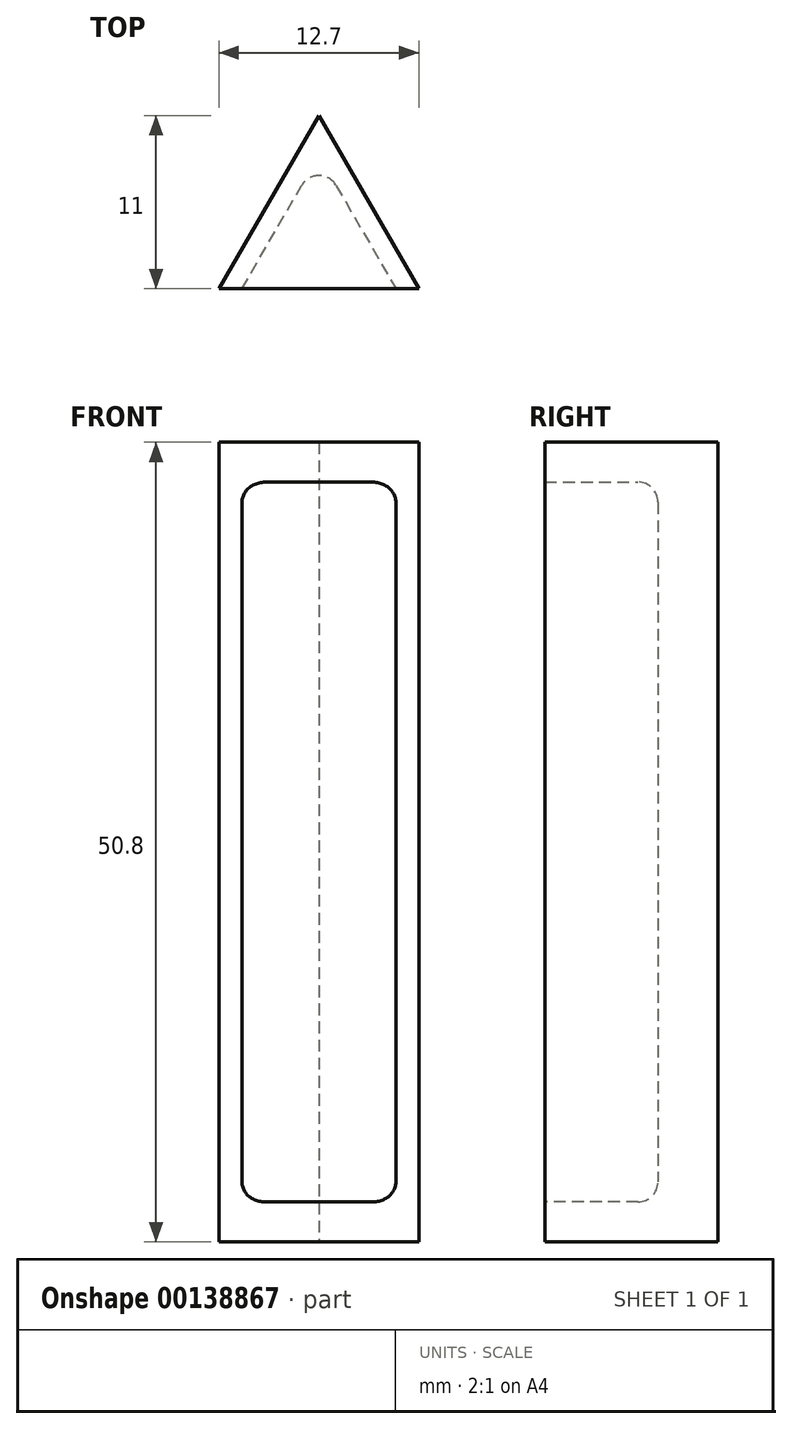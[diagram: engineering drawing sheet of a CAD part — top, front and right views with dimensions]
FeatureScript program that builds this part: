
annotation { "Feature Type Name" : "Feature", "Feature Type Description" : "" }
export const myFeature = defineFeature(function(context is Context, id is Id, definition is map)
    precondition{}
    {
        {
            var Q0;
            Q0=qCreatedBy(makeId("Top.planeOp"),FACE);
            var sketch = newSketch(context, id + "F0", { "sketchPlane" : qUnion([Q0])});
            skLineSegment(sketch, "E0", {"start": v(0, 0) * mm, "end": v(0, 11) * mm});
            skLineSegment(sketch, "E1", {"start": v(0, 11) * mm, "end": v(6.35, 0) * mm});
            skLineSegment(sketch, "E2", {"start": v(6.35, 0) * mm, "end": v(-6.35, 0) * mm});
            skLineSegment(sketch, "E3", {"start": v(-6.35, 0) * mm, "end": v(0, 11) * mm});
            skSolve(sketch);
        }
        {
            var Q0;
            {var subQ0=sQuery(id+"F0.wireOp",EDGE,"E0");Q0=makeQuery(id+"F0.imprint","IMPRINT",FACE,{"disambiguationData":[TD([[makeQuery(id+"F0.imprint","IMPRINT",EDGE,{"derivedFrom":subQ0}),1.0]])]});}
            var Q1;
            {var subQ0=sQuery(id+"F0.wireOp",EDGE,"E0");Q1=makeQuery(id+"F0.imprint","IMPRINT",FACE,{"disambiguationData":[TD([[makeQuery(id+"F0.imprint","IMPRINT",EDGE,{"derivedFrom":subQ0}),-1.0]])]});}
            extrude(context, id + "F1", {"entities" : qUnion([Q0, Q1]), "depth" : 50.8 * mm});
        }
        {
            var Q0;
            Q0=makeQuery(id+"F1.opExtrude","CAP_FACE",FACE,{"disambiguationData":[OSD([sQuery(id+"F0.wireOp",EDGE,"E1"),sQuery(id+"F0.wireOp",EDGE,"E2"),sQuery(id+"F0.wireOp",EDGE,"E3")])],"isStart":false});
            cPlane(context, id + "F2", {"entities" : qUnion([Q0]), "cplaneType" : CPlaneType.OFFSET, "offset" : 2.54 * mm, "oppositeDirection" : true, "width" : 152.4 * mm, "height" : 152.4 * mm});
        }
        {
            var Q0;
            Q0=qCreatedBy(id+"F2.planeOp",FACE);
            var sketch = newSketch(context, id + "F3", { "sketchPlane" : qUnion([Q0])});
            skLineSegment(sketch, "E4.0", {"start": v(-4.15, 1.27) * mm, "end": v(0, 8.46) * mm});
            skLineSegment(sketch, "E4.1", {"start": v(4.15, 1.27) * mm, "end": v(-4.15, 1.27) * mm});
            skLineSegment(sketch, "E4.2", {"start": v(0, 8.46) * mm, "end": v(4.15, 1.27) * mm});
            skLineSegment(sketch, "E5", {"start": v(-4.15, 1.27) * mm, "end": v(-4.88, 0) * mm});
            skLineSegment(sketch, "E6", {"start": v(-4.88, 0) * mm, "end": v(4.88, 0) * mm});
            skLineSegment(sketch, "E7", {"start": v(4.88, 0) * mm, "end": v(4.15, 1.27) * mm});
            skSolve(sketch);
        }
        {
            var Q0;
            Q0=makeQuery(id+"F3.imprint","IMPRINT",FACE,{"disambiguationData":[TD([[makeQuery(id+"F3.imprint","IMPRINT",EDGE,{"derivedFrom":sQuery(id+"F3.wireOp",EDGE,"E4.0")}),-1.0]])]});
            var Q1;
            Q1=makeQuery(id+"F3.imprint","IMPRINT",FACE,{"disambiguationData":[TD([[makeQuery(id+"F3.imprint","IMPRINT",EDGE,{"derivedFrom":sQuery(id+"F3.wireOp",EDGE,"E4.1")}),1.0]])]});
            extrude(context, id + "F4", {"entities" : qUnion([Q0, Q1]), "operationType" : NewBodyOperationType.REMOVE, "oppositeDirection" : true, "depth" : 45.72 * mm});
        }
        {
            var Q0;
            Q0=makeQuery(id+"F4.boolean.opBoolean","COPY",EDGE,{"derivedFrom":makeQuery(id+"F4.opExtrude","SWEPT_EDGE",EDGE,{"disambiguationData":[OSD([sQuery(id+"F3.wireOp",EDGE,"E4.0"),sQuery(id+"F3.wireOp",EDGE,"E4.2")])]})});
            var Q1;
            Q1=makeQuery(id+"F4.boolean.opBoolean","COPY",EDGE,{"derivedFrom":makeQuery(id+"F4.opExtrude","CAP_EDGE",EDGE,{"disambiguationData":[OSD([sQuery(id+"F3.wireOp",EDGE,"E4.2"),sQuery(id+"F3.wireOp",EDGE,"E7")])],"isStart":false})});
            var Q2;
            Q2=makeQuery(id+"F4.boolean.opBoolean","COPY",EDGE,{"derivedFrom":makeQuery(id+"F4.opExtrude","CAP_EDGE",EDGE,{"disambiguationData":[OSD([sQuery(id+"F3.wireOp",EDGE,"E4.0"),sQuery(id+"F3.wireOp",EDGE,"E5")])],"isStart":false})});
            var Q3;
            Q3=makeQuery(id+"F4.boolean.opBoolean","COPY",EDGE,{"derivedFrom":makeQuery(id+"F4.opExtrude","CAP_EDGE",EDGE,{"disambiguationData":[OSD([sQuery(id+"F3.wireOp",EDGE,"E4.0"),sQuery(id+"F3.wireOp",EDGE,"E5")])],"isStart":true})});
            var Q4;
            Q4=makeQuery(id+"F4.boolean.opBoolean","COPY",EDGE,{"derivedFrom":makeQuery(id+"F4.opExtrude","CAP_EDGE",EDGE,{"disambiguationData":[OSD([sQuery(id+"F3.wireOp",EDGE,"E4.2"),sQuery(id+"F3.wireOp",EDGE,"E7")])],"isStart":true})});
            fillet(context, id + "F5", {"entities" : qUnion([Q0, Q1, Q2, Q3, Q4]), "radius" : 1.27 * mm, "tangentPropagation" : true, "allowEdgeOverflow" : false});
        }
    });
